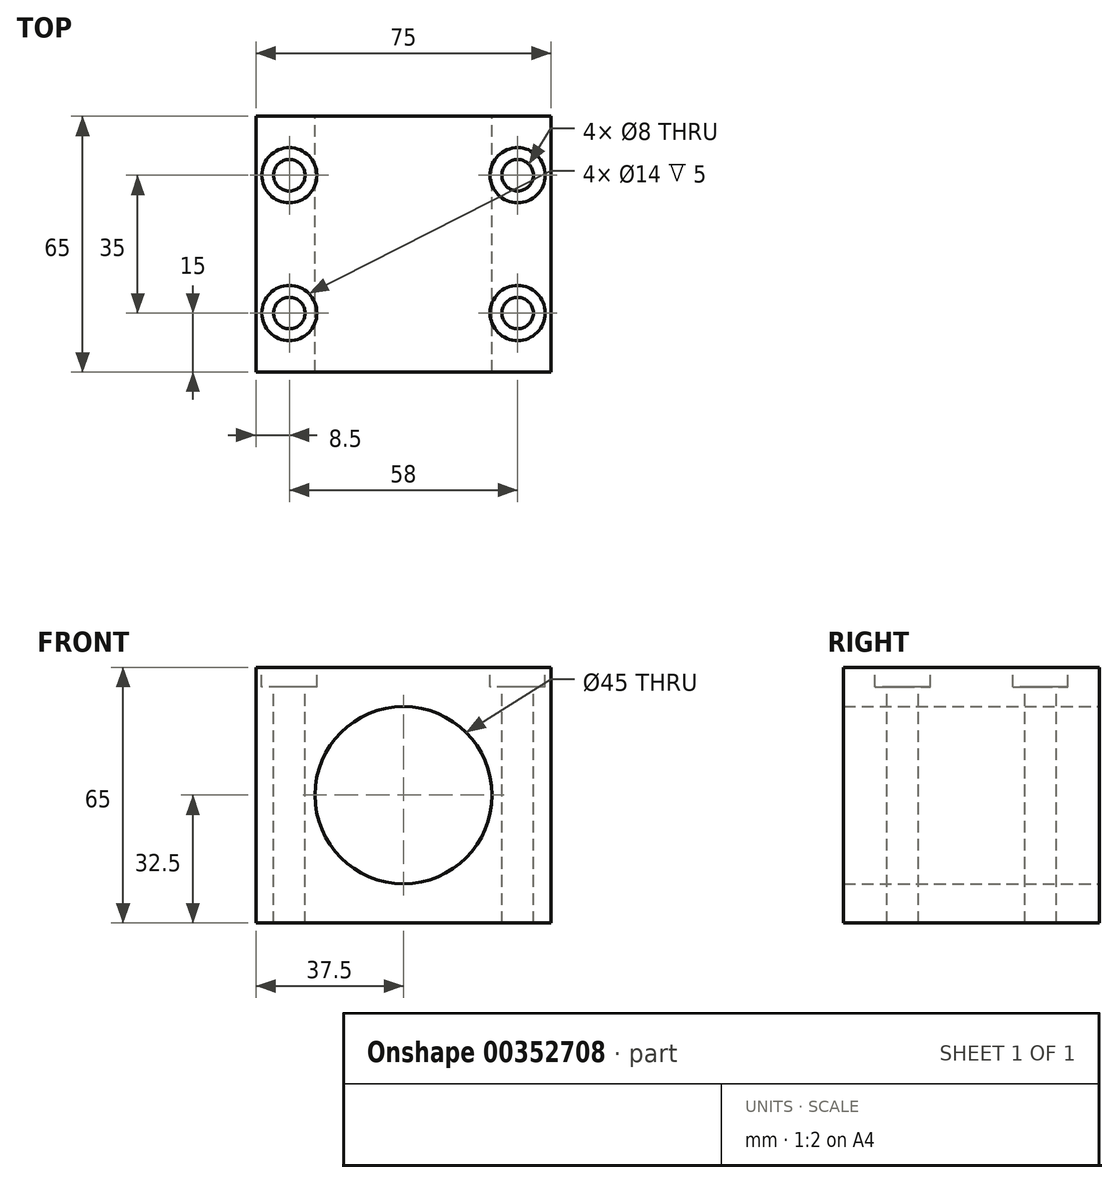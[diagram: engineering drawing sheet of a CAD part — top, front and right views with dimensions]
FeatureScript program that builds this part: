
annotation { "Feature Type Name" : "Feature", "Feature Type Description" : "" }
export const myFeature = defineFeature(function(context is Context, id is Id, definition is map)
    precondition{}
    {
        {
            var Q0;
            Q0=qCreatedBy(makeId("Front.planeOp"),FACE);
            var sketch = newSketch(context, id + "F0", { "sketchPlane" : qUnion([Q0])});
            skLineSegment(sketch, "E0.bottom", {"start": v(0, 0) * mm, "end": v(75, 0) * mm});
            skLineSegment(sketch, "E0.top", {"start": v(0, 65) * mm, "end": v(75, 65) * mm});
            skLineSegment(sketch, "E0.left", {"start": v(0, 0) * mm, "end": v(0, 65) * mm});
            skLineSegment(sketch, "E0.right", {"start": v(75, 0) * mm, "end": v(75, 65) * mm});
            skLineSegment(sketch, "E1", {"start": v(37.5, 100.71) * mm, "end": v(37.5, -30.58) * mm, "construction": true});
            skLineSegment(sketch, "E2", {"start": v(-27, 32.5) * mm, "end": v(126.1, 32.5) * mm, "construction": true});
            skCircle(sketch, "E3", {"center": v(37.5, 32.5) * mm, "radius": 22.5 * mm});
            skPoint(sketch, "E3.centerSnap0", {"position": v(37.5, 35.07) * mm});
            skLineSegment(sketch, "E4", {"start": v(7.5, 86.6) * mm, "end": v(7.5, -14.57) * mm, "construction": true});
            skLineSegment(sketch, "E5", {"start": v(67.5, 87.07) * mm, "end": v(67.5, -18.45) * mm, "construction": true});
            skSolve(sketch);
        }
        {
            var Q0;
            Q0 = qSketchRegion(id + "F0", true);
            extrude(context, id + "F1", {"entities" : qUnion([Q0]), "endBound" : BoundingType.SYMMETRIC, "depth" : 65 * mm});
        }
        {
            var Q0;
            Q0=makeQuery(id+"F1.opExtrude","SWEPT_FACE",FACE,{"disambiguationData":[OSD([sQuery(id+"F0.wireOp",EDGE,"E0.top")])]});
            var sketch = newSketch(context, id + "F2", { "sketchPlane" : qUnion([Q0])});
            skLineSegment(sketch, "E6", {"start": v(8.5, 43.93) * mm, "end": v(8.5, -38.42) * mm, "construction": true});
            skLineSegment(sketch, "E7", {"start": v(66.5, 46.47) * mm, "end": v(66.5, -39.33) * mm, "construction": true});
            skLineSegment(sketch, "E8", {"start": v(-7.07, 17.5) * mm, "end": v(103.33, 17.5) * mm, "construction": true});
            skLineSegment(sketch, "E9", {"start": v(-7.65, -17.5) * mm, "end": v(96.19, -17.5) * mm, "construction": true});
            skCircle(sketch, "E10", {"center": v(8.5, 17.5) * mm, "radius": 4 * mm});
            skCircle(sketch, "E11", {"center": v(66.5, 17.5) * mm, "radius": 4 * mm});
            skCircle(sketch, "E12", {"center": v(66.5, -17.5) * mm, "radius": 4 * mm});
            skCircle(sketch, "E13", {"center": v(8.5, -17.5) * mm, "radius": 4 * mm});
            skCircle(sketch, "E14", {"center": v(8.5, 17.5) * mm, "radius": 7 * mm});
            skCircle(sketch, "E15", {"center": v(66.5, 17.5) * mm, "radius": 7 * mm});
            skCircle(sketch, "E16", {"center": v(8.5, -17.5) * mm, "radius": 7 * mm});
            skCircle(sketch, "E17", {"center": v(66.5, -17.5) * mm, "radius": 7 * mm});
            skSolve(sketch);
        }
        {
            var Q0;
            Q0=makeQuery(id+"F2.imprint","IMPRINT",FACE,{"disambiguationData":[TD([[makeQuery(id+"F2.imprint","IMPRINT",EDGE,{"derivedFrom":sQuery(id+"F2.wireOp",EDGE,"E11")}),1.0]])]});
            var Q1;
            Q1=makeQuery(id+"F2.imprint","IMPRINT",FACE,{"disambiguationData":[TD([[makeQuery(id+"F2.imprint","IMPRINT",EDGE,{"derivedFrom":sQuery(id+"F2.wireOp",EDGE,"E12")}),1.0]])]});
            var Q2;
            Q2=makeQuery(id+"F2.imprint","IMPRINT",FACE,{"disambiguationData":[TD([[makeQuery(id+"F2.imprint","IMPRINT",EDGE,{"derivedFrom":sQuery(id+"F2.wireOp",EDGE,"E13")}),1.0]])]});
            var Q3;
            Q3=makeQuery(id+"F2.imprint","IMPRINT",FACE,{"disambiguationData":[TD([[makeQuery(id+"F2.imprint","IMPRINT",EDGE,{"derivedFrom":sQuery(id+"F2.wireOp",EDGE,"E10")}),1.0]])]});
            extrude(context, id + "F3", {"entities" : qUnion([Q0, Q1, Q2, Q3]), "operationType" : NewBodyOperationType.REMOVE, "endBound" : BoundingType.THROUGH_ALL, "oppositeDirection" : true, "depth" : 25 * mm});
        }
        {
            var Q0;
            Q0=makeQuery(id+"F2.imprint","IMPRINT",FACE,{"disambiguationData":[TD([[makeQuery(id+"F2.imprint","IMPRINT",EDGE,{"derivedFrom":sQuery(id+"F2.wireOp",EDGE,"E10")}),-1.0]])]});
            var Q1;
            Q1=makeQuery(id+"F2.imprint","IMPRINT",FACE,{"disambiguationData":[TD([[makeQuery(id+"F2.imprint","IMPRINT",EDGE,{"derivedFrom":sQuery(id+"F2.wireOp",EDGE,"E11")}),-1.0]])]});
            var Q2;
            Q2=makeQuery(id+"F2.imprint","IMPRINT",FACE,{"disambiguationData":[TD([[makeQuery(id+"F2.imprint","IMPRINT",EDGE,{"derivedFrom":sQuery(id+"F2.wireOp",EDGE,"E12")}),-1.0]])]});
            var Q3;
            Q3=makeQuery(id+"F2.imprint","IMPRINT",FACE,{"disambiguationData":[TD([[makeQuery(id+"F2.imprint","IMPRINT",EDGE,{"derivedFrom":sQuery(id+"F2.wireOp",EDGE,"E13")}),-1.0]])]});
            extrude(context, id + "F4", {"entities" : qUnion([Q0, Q1, Q2, Q3]), "operationType" : NewBodyOperationType.REMOVE, "oppositeDirection" : true, "depth" : 5 * mm});
        }
    });
